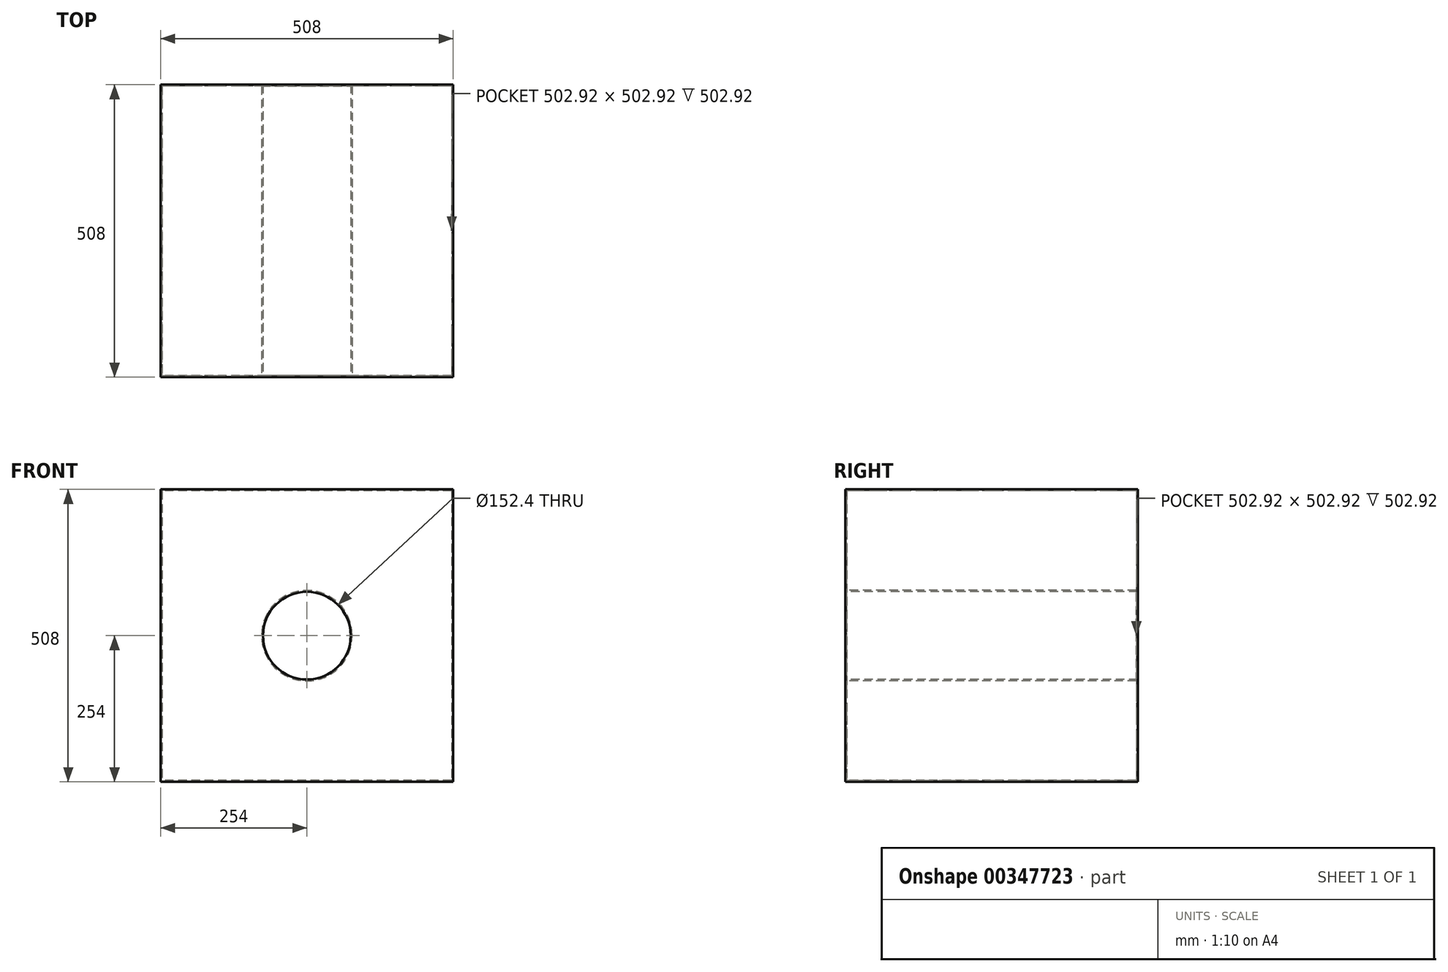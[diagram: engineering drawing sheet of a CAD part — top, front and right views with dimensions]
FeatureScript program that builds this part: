
annotation { "Feature Type Name" : "Feature", "Feature Type Description" : "" }
export const myFeature = defineFeature(function(context is Context, id is Id, definition is map)
    precondition{}
    {
        {
            var Q0;
            Q0=qCreatedBy(makeId("Top.planeOp"),FACE);
            var sketch = newSketch(context, id + "F0", { "sketchPlane" : qUnion([Q0])});
            skLineSegment(sketch, "E0.bottom", {"start": v(254, 254) * mm, "end": v(-254, 254) * mm});
            skLineSegment(sketch, "E0.top", {"start": v(254, -254) * mm, "end": v(-254, -254) * mm});
            skLineSegment(sketch, "E0.left", {"start": v(254, 254) * mm, "end": v(254, -254) * mm});
            skLineSegment(sketch, "E0.right", {"start": v(-254, 254) * mm, "end": v(-254, -254) * mm});
            skPoint(sketch, "E0.middle", {"position": v(0, 0) * mm});
            skSolve(sketch);
        }
        {
            var Q0;
            Q0 = qSketchRegion(id + "F0", true);
            extrude(context, id + "F1", {"entities" : qUnion([Q0]), "depth" : 508 * mm});
        }
        {
            var Q0;
            Q0=makeQuery(id+"F1.opExtrude","SWEPT_FACE",FACE,{"disambiguationData":[OSD([sQuery(id+"F0.wireOp",EDGE,"E0.top")])]});
            var sketch = newSketch(context, id + "F2", { "sketchPlane" : qUnion([Q0])});
            skCircle(sketch, "E1", {"center": v(0, 254) * mm, "radius": 76.2 * mm});
            skSolve(sketch);
        }
        {
            var Q0;
            Q0=sQuery(id+"F2.wireOp",VERTEX,"E1.center");
            var Q1;
            Q1=makeQuery(id+"F1.opExtrude","SWEPT_BODY",BODY,{"disambiguationData":[OSD([sQuery(id+"F0.wireOp",EDGE,"E0.bottom"),sQuery(id+"F0.wireOp",EDGE,"E0.top"),sQuery(id+"F0.wireOp",EDGE,"E0.left"),sQuery(id+"F0.wireOp",EDGE,"E0.right")])]});
            hole(context, id + "F3", {"style" : HoleStyle.SIMPLE, "endStyle" : HoleEndStyle.THROUGH, "holeDiameter" : 152.4 * mm, "isTappedThrough" : true, "tappedDepth" : 12.7 * mm, "tapClearance" : 3, "locations" : qUnion([Q0]), "scope" : qUnion([Q1])});
        }
        {
            var Q0;
            Q0=makeQuery(id+"F1.opExtrude","SWEPT_FACE",FACE,{"disambiguationData":[OSD([sQuery(id+"F0.wireOp",EDGE,"E0.top")])]});
            var Q1;
            Q1=makeQuery(id+"F1.opExtrude","SWEPT_BODY",BODY,{"disambiguationData":[OSD([sQuery(id+"F0.wireOp",EDGE,"E0.bottom"),sQuery(id+"F0.wireOp",EDGE,"E0.top"),sQuery(id+"F0.wireOp",EDGE,"E0.left"),sQuery(id+"F0.wireOp",EDGE,"E0.right")])]});
            shell(context, id + "F4", {"isHollow" : true, "entities" : qUnion([Q0]), "parts" : qUnion([Q1]), "thickness" : 2.54 * mm});
        }
    });
